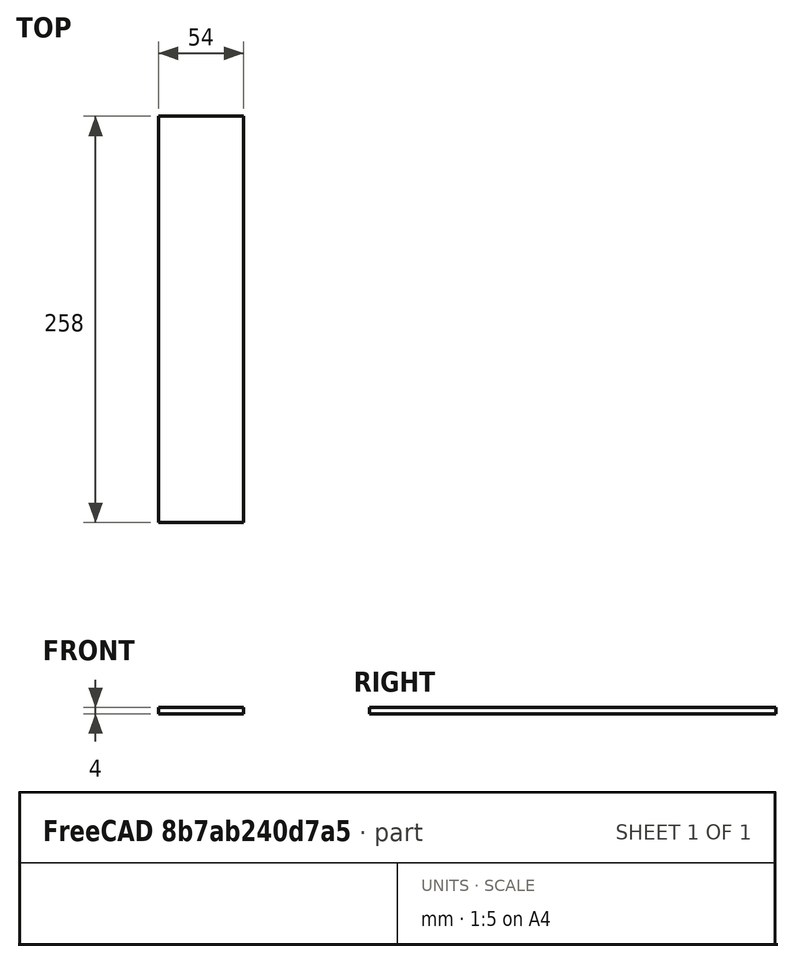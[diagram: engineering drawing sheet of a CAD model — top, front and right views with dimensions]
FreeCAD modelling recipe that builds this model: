
FCSTD DOCUMENT  (FreeCAD 0.17R13528 (Git))
Label: GlassDarkSide
License: All rights reserved
LicenseURL: http://en.wikipedia.org/wiki/All_rights_reserved
objects: Sketcher::SketchObject×1, PartDesign::Pad×1, PartDesign::Body×1
note: 4 computed .brp shape members not serialized (recipe doc carries the construction recipe); baked Part::Feature solids carry a one-line shape summary decoded from their .brp

FEATURE [Sketcher::SketchObject] Sketch
  MapMode = 5
  Support = -> [XY_Plane]
  expr: Constraints[10] = 50 + 4
  sketch-geometry (4):
    g0: LineSegment StartX=0 StartY=0 StartZ=0 EndX=54 EndY=0 EndZ=0
    g1: LineSegment StartX=54 StartY=0 StartZ=0 EndX=54 EndY=258 EndZ=0
    g2: LineSegment StartX=54 StartY=258 StartZ=0 EndX=0 EndY=258 EndZ=0
    g3: LineSegment StartX=0 StartY=258 StartZ=0 EndX=0 EndY=0 EndZ=0
  constraints (11):
    c: Coincident(g0,g1)
    c: Coincident(g1,g2)
    c: Coincident(g2,g3)
    c: Coincident(g3,g0)
    c: Horizontal(g0)
    c: Horizontal(g2)
    c: Vertical(g1)
    c: Vertical(g3)
    c: Coincident(g0,g-1)
    c: DistanceY(g3,g3) = 258
    c: DistanceX(g0,g0) = 54
FEATURE [PartDesign::Pad] Pad
  Length = 4
  Length2 = 100
  Profile = -> Sketch
  Type = 0
  expr: Length = Data#Spreadsheet.B1
FEATURE [PartDesign::Body] Body
  Group = -> [Sketch,Pad]
  Origin = -> Origin
  Tip = -> Pad
